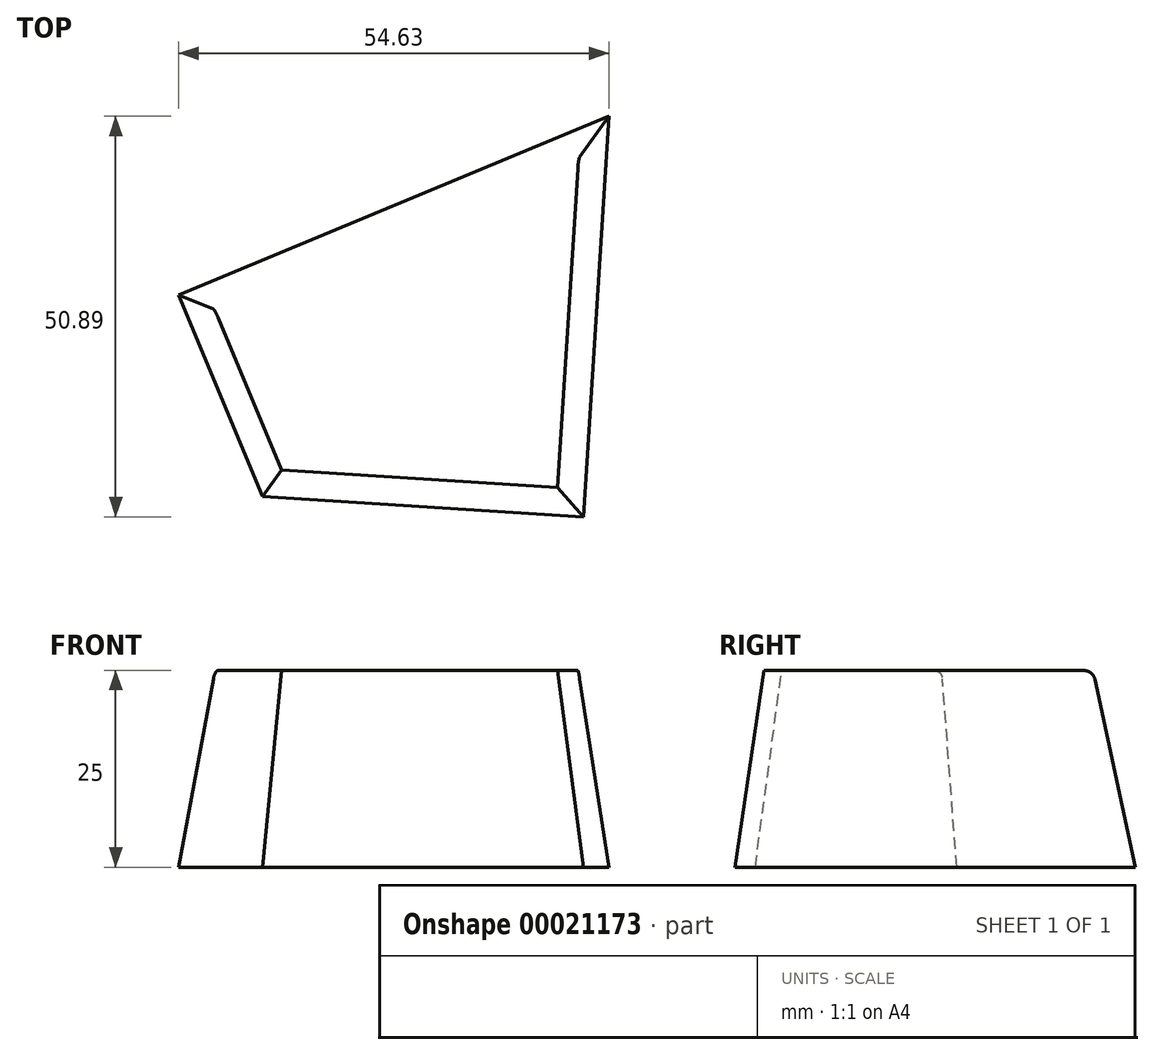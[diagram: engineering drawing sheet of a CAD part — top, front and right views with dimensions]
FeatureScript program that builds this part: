
annotation { "Feature Type Name" : "Feature", "Feature Type Description" : "" }
export const myFeature = defineFeature(function(context is Context, id is Id, definition is map)
    precondition{}
    {
        {
            var Q0;
            Q0=qCreatedBy(makeId("Top.planeOp"),FACE);
            var sketch = newSketch(context, id + "F0", { "sketchPlane" : qUnion([Q0])});
            skLineSegment(sketch, "E0", {"start": v(0, 0) * mm, "end": v(46.17, 19.18) * mm});
            skLineSegment(sketch, "E1", {"start": v(46.17, 19.18) * mm, "end": v(43.52, -22.57) * mm});
            skLineSegment(sketch, "E2", {"start": v(43.52, -22.57) * mm, "end": v(8.45, -20.34) * mm});
            skLineSegment(sketch, "E3", {"start": v(8.45, -20.34) * mm, "end": v(0, 0) * mm});
            skSolve(sketch);
        }
        {
            var Q0;
            Q0=makeQuery(id+"F0.imprint","IMPRINT",FACE,{"disambiguationData":[TD([[makeQuery(id+"F0.imprint","IMPRINT",EDGE,{"derivedFrom":sQuery(id+"F0.wireOp",EDGE,"E0")}),-1.0]])]});
            extrude(context, id + "F1", {"entities" : qUnion([Q0]), "oppositeDirection" : true, "depth" : 25 * mm, "hasDraft" : true, "draftAngle" : 8 * degree});
        }
        {
            var Q0;
            Q0=makeQuery(id+"F1.opExtrude","CAP_EDGE",EDGE,{"disambiguationData":[OSD([sQuery(id+"F0.wireOp",EDGE,"E0")])],"isStart":true});
            fillet(context, id + "F2", {"entities" : qUnion([Q0]), "radius" : 1.25 * mm, "tangentPropagation" : true, "allowEdgeOverflow" : false});
        }
    });
